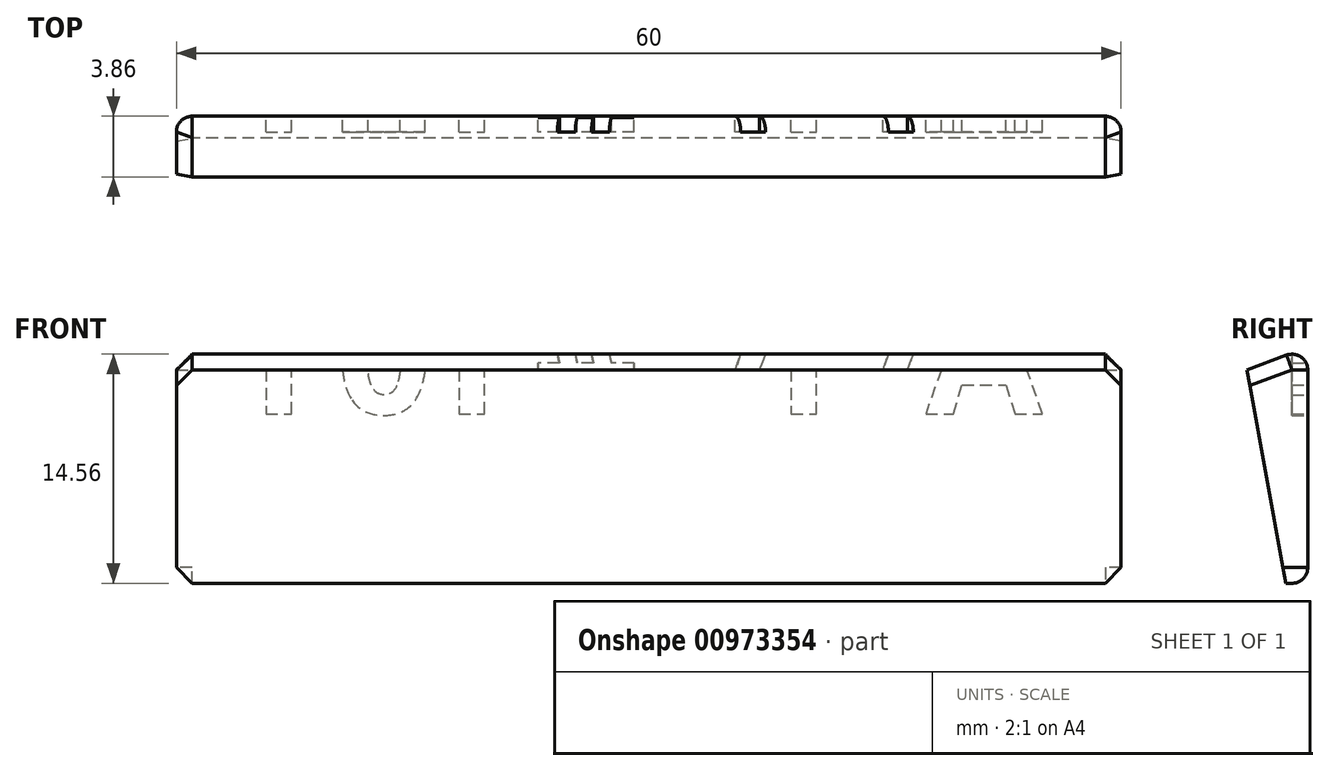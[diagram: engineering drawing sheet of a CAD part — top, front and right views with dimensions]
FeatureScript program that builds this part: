
annotation { "Feature Type Name" : "Feature", "Feature Type Description" : "" }
export const myFeature = defineFeature(function(context is Context, id is Id, definition is map)
    precondition{}
    {
        {
            var Q0;
            Q0=qCreatedBy(makeId("Right.planeOp"),FACE);
            var sketch = newSketch(context, id + "F0", { "sketchPlane" : qUnion([Q0])});
            skLineSegment(sketch, "E0.0", {"start": v(14.23, 15) * mm, "end": v(14.23, 0) * mm});
            skLineSegment(sketch, "E0.2", {"start": v(-25.77, 0) * mm, "end": v(14.23, 15) * mm});
            skPoint(sketch, "E0.0.midPoint", {"position": v(14.23, 0) * mm});
            skLineSegment(sketch, "E1", {"start": v(-25.77, 0) * mm, "end": v(14.23, 0) * mm});
            skPoint(sketch, "E2.orphan", {"position": v(14.23, -15) * mm});
            skSolve(sketch);
        }
        {
            var Q0;
            Q0=makeQuery(id+"F0.imprint","IMPRINT",FACE,{"disambiguationData":[TD([[makeQuery(id+"F0.imprint","IMPRINT",EDGE,{"derivedFrom":sQuery(id+"F0.wireOp",EDGE,"E0.0")}),-1.0]])]});
            extrude(context, id + "F1", {"entities" : qUnion([Q0]), "depth" : 60 * mm, "offsetDistance" : 25 * mm, "symmetric" : true});
        }
        {
            var Q0;
            Q0=makeQuery(id+"F1.opExtrude","SWEPT_EDGE",EDGE,{"disambiguationData":[OSD([sQuery(id+"F0.wireOp",EDGE,"E0.0"),sQuery(id+"F0.wireOp",EDGE,"E0.2")])]});
            var Q1;
            Q1=makeQuery(id+"F1.opExtrude","CAP_EDGE",EDGE,{"disambiguationData":[OSD([sQuery(id+"F0.wireOp",EDGE,"E0.0")])],"isStart":false});
            var Q2;
            Q2=makeQuery(id+"F1.opExtrude","CAP_EDGE",EDGE,{"disambiguationData":[OSD([sQuery(id+"F0.wireOp",EDGE,"E0.0")])],"isStart":true});
            var Q3;
            Q3=makeQuery(id+"F1.opExtrude","SWEPT_EDGE",EDGE,{"disambiguationData":[OSD([sQuery(id+"F0.wireOp",EDGE,"E0.0"),sQuery(id+"F0.wireOp",EDGE,"E1")])]});
            fillet(context, id + "F2", {"entities" : qUnion([Q0, Q1, Q2, Q3]), "tangentPropagation" : true, "radius" : 1 * mm, "defaultsChanged" : false, "vertexSettings" : [], "allowEdgeOverflow" : false});
        }
        {
            var Q0;
            Q0=makeQuery(id+"F1.opExtrude","CAP_EDGE",EDGE,{"disambiguationData":[OSD([sQuery(id+"F0.wireOp",EDGE,"E0.2")])],"isStart":true});
            var Q1;
            Q1=makeQuery(id+"F1.opExtrude","CAP_EDGE",EDGE,{"disambiguationData":[OSD([sQuery(id+"F0.wireOp",EDGE,"E1")])],"isStart":false});
            var Q2;
            Q2=makeQuery(id+"F1.opExtrude","CAP_EDGE",EDGE,{"disambiguationData":[OSD([sQuery(id+"F0.wireOp",EDGE,"E0.2")])],"isStart":false});
            var Q3;
            Q3=makeQuery(id+"F1.opExtrude","CAP_EDGE",EDGE,{"disambiguationData":[OSD([sQuery(id+"F0.wireOp",EDGE,"E1")])],"isStart":true});
            chamfer(context, id + "F3", {"entities" : qUnion([Q0, Q1, Q2, Q3]), "width" : 1 * mm, "tangentPropagation" : true});
        }
        {
            var Q0;
            Q0=makeQuery(id+"F1.opExtrude","SWEPT_EDGE",EDGE,{"disambiguationData":[OSD([sQuery(id+"F0.wireOp",EDGE,"E0.2"),sQuery(id+"F0.wireOp",EDGE,"E1")])]});
            chamfer(context, id + "F4", {"entities" : qUnion([Q0]), "width" : 7 * mm, "tangentPropagation" : true});
        }
        {
            var Q0;
            Q0=makeQuery(id+"F1.opExtrude","SWEPT_FACE",FACE,{"disambiguationData":[OSD([sQuery(id+"F0.wireOp",EDGE,"E0.0")])]});
            var sketch = newSketch(context, id + "F5", { "sketchPlane" : qUnion([Q0])});
            skPoint(sketch, "E3", {"position": v(0, 7.28) * mm});
            skPoint(sketch, "E4.orphan", {"position": v(0, 1) * mm});
            skPoint(sketch, "E5.start.orphan", {"position": v(0, 13.56) * mm});
            skText(sketch, "E6", { "text": "Aviv #101", "fontName": "OpenSans-Bold.ttf"});
            const initialGuessF5  = {"E6": [-0.025, 0.01077, 1, 0, 0.00773]};
            skSetInitialGuess(sketch, initialGuessF5);
            skSolve(sketch);
        }
        {
            var Q0;
            Q0=makeQuery(id+"F5.imprint","IMPRINT",FACE,{"disambiguationData":[TD([[makeQuery(id+"F5.imprint","IMPRINT",EDGE,{"derivedFrom":sQuery(id+"F5.wireOp",EDGE,"E6.sketch_text.stroke-99")}),-1.0]])]});
            var Q1;
            Q1=makeQuery(id+"F5.imprint","IMPRINT",FACE,{"disambiguationData":[TD([[makeQuery(id+"F5.imprint","IMPRINT",EDGE,{"derivedFrom":sQuery(id+"F5.wireOp",EDGE,"E6.sketch_text.stroke-83")}),-1.0]])]});
            var Q2;
            Q2=makeQuery(id+"F5.imprint","IMPRINT",FACE,{"disambiguationData":[TD([[makeQuery(id+"F5.imprint","IMPRINT",EDGE,{"derivedFrom":sQuery(id+"F5.wireOp",EDGE,"E6.sketch_text.stroke-73")}),-1.0]])]});
            var Q3;
            Q3=makeQuery(id+"F5.imprint","IMPRINT",FACE,{"disambiguationData":[TD([[makeQuery(id+"F5.imprint","IMPRINT",EDGE,{"derivedFrom":sQuery(id+"F5.wireOp",EDGE,"E6.sketch_text.stroke-41")}),-1.0]])]});
            var Q4;
            Q4=makeQuery(id+"F5.imprint","IMPRINT",FACE,{"disambiguationData":[TD([[makeQuery(id+"F5.imprint","IMPRINT",EDGE,{"derivedFrom":sQuery(id+"F5.wireOp",EDGE,"E6.sketch_text.stroke-27")}),-1.0]])]});
            var Q5;
            Q5=makeQuery(id+"F5.imprint","IMPRINT",FACE,{"disambiguationData":[TD([[makeQuery(id+"F5.imprint","IMPRINT",EDGE,{"derivedFrom":sQuery(id+"F5.wireOp",EDGE,"E6.sketch_text.stroke-31")}),-1.0]])]});
            var Q6;
            Q6=makeQuery(id+"F5.imprint","IMPRINT",FACE,{"disambiguationData":[TD([[makeQuery(id+"F5.imprint","IMPRINT",EDGE,{"derivedFrom":sQuery(id+"F5.wireOp",EDGE,"E6.sketch_text.stroke-22")}),-1.0]])]});
            var Q7;
            Q7=makeQuery(id+"F5.imprint","IMPRINT",FACE,{"disambiguationData":[TD([[makeQuery(id+"F5.imprint","IMPRINT",EDGE,{"derivedFrom":sQuery(id+"F5.wireOp",EDGE,"E6.sketch_text.stroke-12")}),-1.0]])]});
            var Q8;
            Q8=makeQuery(id+"F5.imprint","IMPRINT",FACE,{"disambiguationData":[TD([[makeQuery(id+"F5.imprint","IMPRINT",EDGE,{"derivedFrom":sQuery(id+"F5.wireOp",EDGE,"E6.sketch_text.stroke-0")}),-1.0]])]});
            extrude(context, id + "F6", {"entities" : qUnion([Q0, Q1, Q2, Q3, Q4, Q5, Q6, Q7, Q8]), "operationType" : NewBodyOperationType.REMOVE, "oppositeDirection" : true, "depth" : 1 * mm, "offsetDistance" : 25 * mm});
        }
    });
